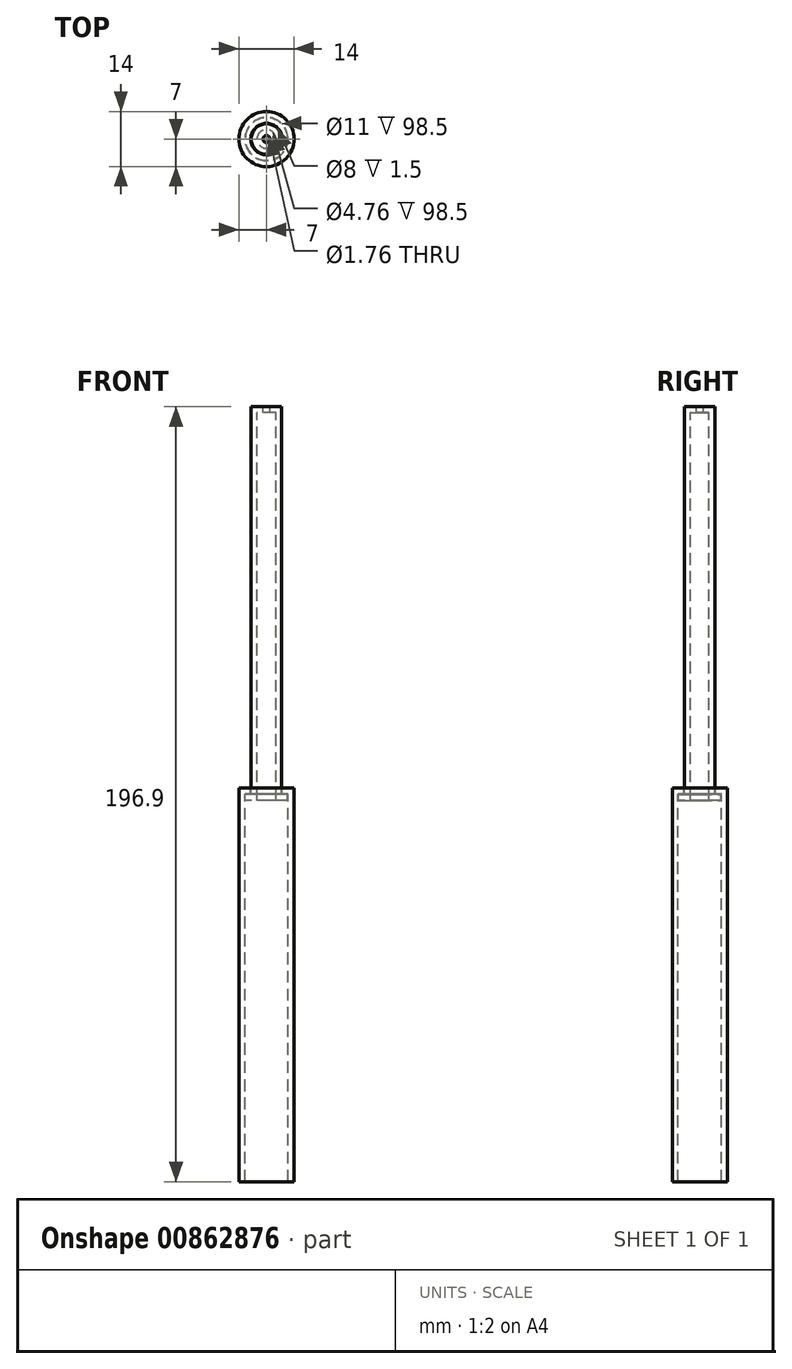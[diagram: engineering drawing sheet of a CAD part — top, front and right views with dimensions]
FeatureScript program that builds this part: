
annotation { "Feature Type Name" : "Feature", "Feature Type Description" : "" }
export const myFeature = defineFeature(function(context is Context, id is Id, definition is map)
    precondition{}
    {
        {
            var Q0;
            Q0=qCreatedBy(makeId("Front.planeOp"),FACE);
            var sketch = newSketch(context, id + "F0", { "sketchPlane" : qUnion([Q0])});
            skLineSegment(sketch, "E0.bottom", {"start": v(-7, 0) * mm, "end": v(-4, 0) * mm});
            skLineSegment(sketch, "E0.top", {"start": v(-7, -100) * mm, "end": v(-5.5, -100) * mm});
            skLineSegment(sketch, "E0.left", {"start": v(-7, 0) * mm, "end": v(-7, -100) * mm});
            skLineSegment(sketch, "E0.right", {"start": v(7, 0) * mm, "end": v(7, -100) * mm});
            skLineSegment(sketch, "E1.0", {"start": v(5.5, -1.5) * mm, "end": v(5.5, -100) * mm});
            skLineSegment(sketch, "E1.1", {"start": v(-5.5, -1.5) * mm, "end": v(-4, -1.5) * mm});
            skLineSegment(sketch, "E1.2", {"start": v(-5.5, -1.5) * mm, "end": v(-5.5, -100) * mm});
            skLineSegment(sketch, "E2.trimOffspring", {"start": v(5.5, -100) * mm, "end": v(7, -100) * mm});
            skLineSegment(sketch, "E3", {"start": v(4, 0) * mm, "end": v(4, -1.5) * mm});
            skLineSegment(sketch, "E4", {"start": v(-4, 0) * mm, "end": v(-4, -1.5) * mm});
            skLineSegment(sketch, "E5.trimOffspring", {"start": v(4, 0) * mm, "end": v(7, 0) * mm});
            skLineSegment(sketch, "E6.trimOffspring", {"start": v(4, -1.5) * mm, "end": v(5.5, -1.5) * mm});
            skLineSegment(sketch, "E7", {"start": v(0, 0) * mm, "end": v(0, -115.14) * mm, "construction": true});
            skLineSegment(sketch, "E8.bottom", {"start": v(-3.88, -3.1) * mm, "end": v(-2.38, -3.1) * mm});
            skLineSegment(sketch, "E8.top", {"start": v(-3.88, 96.9) * mm, "end": v(-0.88, 96.9) * mm});
            skLineSegment(sketch, "E8.left", {"start": v(-3.88, -1.6) * mm, "end": v(-3.88, 96.9) * mm});
            skLineSegment(sketch, "E8.right", {"start": v(3.9, -1.6) * mm, "end": v(3.9, 96.9) * mm});
            skLineSegment(sketch, "E9", {"start": v(-3.88, -1.6) * mm, "end": v(-5.4, -1.6) * mm});
            skLineSegment(sketch, "E10", {"start": v(-5.4, -3.1) * mm, "end": v(-3.88, -3.1) * mm});
            skLineSegment(sketch, "E11", {"start": v(-5.4, -1.6) * mm, "end": v(-5.4, -3.1) * mm});
            skLineSegment(sketch, "E12", {"start": v(3.9, -1.6) * mm, "end": v(5.4, -1.6) * mm});
            skLineSegment(sketch, "E13", {"start": v(5.4, -3.1) * mm, "end": v(3.9, -3.1) * mm});
            skLineSegment(sketch, "E14", {"start": v(5.4, -1.6) * mm, "end": v(5.4, -3.1) * mm});
            skLineSegment(sketch, "E15.0", {"start": v(2.4, -3.1) * mm, "end": v(2.4, 95.4) * mm});
            skLineSegment(sketch, "E15.1", {"start": v(-2.38, 95.4) * mm, "end": v(-0.88, 95.4) * mm});
            skLineSegment(sketch, "E15.2", {"start": v(-2.38, -3.1) * mm, "end": v(-2.38, 95.4) * mm});
            skLineSegment(sketch, "E16.trimOffspring", {"start": v(2.4, -3.1) * mm, "end": v(3.9, -3.1) * mm});
            skLineSegment(sketch, "E17", {"start": v(-0.88, 95.4) * mm, "end": v(-0.88, 96.9) * mm});
            skLineSegment(sketch, "E18", {"start": v(0.9, 96.9) * mm, "end": v(0.9, 95.4) * mm});
            skLineSegment(sketch, "E19.trimOffspring", {"start": v(0.9, 96.9) * mm, "end": v(3.9, 96.9) * mm});
            skLineSegment(sketch, "E20.trimOffspring", {"start": v(0.9, 95.4) * mm, "end": v(2.4, 95.4) * mm});
            skSolve(sketch);
        }
        {
            var Q0;
            Q0=makeQuery(id+"F0.imprint","IMPRINT",FACE,{"disambiguationData":[TD([[makeQuery(id+"F0.imprint","IMPRINT",EDGE,{"derivedFrom":sQuery(id+"F0.wireOp",EDGE,"E8.bottom")}),1.0]])]});
            var Q1;
            Q1=makeQuery(id+"F0.imprint","IMPRINT",FACE,{"disambiguationData":[TD([[makeQuery(id+"F0.imprint","IMPRINT",EDGE,{"derivedFrom":sQuery(id+"F0.wireOp",EDGE,"E0.bottom")}),-1.0]])]});
            var Q2;
            Q2=sQuery(id+"F0.wireOp",EDGE,"E7");
            revolve(context, id + "F1", {"surfaceOperationType" : NewSurfaceOperationType.NEW, "entities" : qUnion([Q0, Q1]), "axis" : qUnion([Q2]), "revolveType" : RevolveType.FULL});
        }
    });
